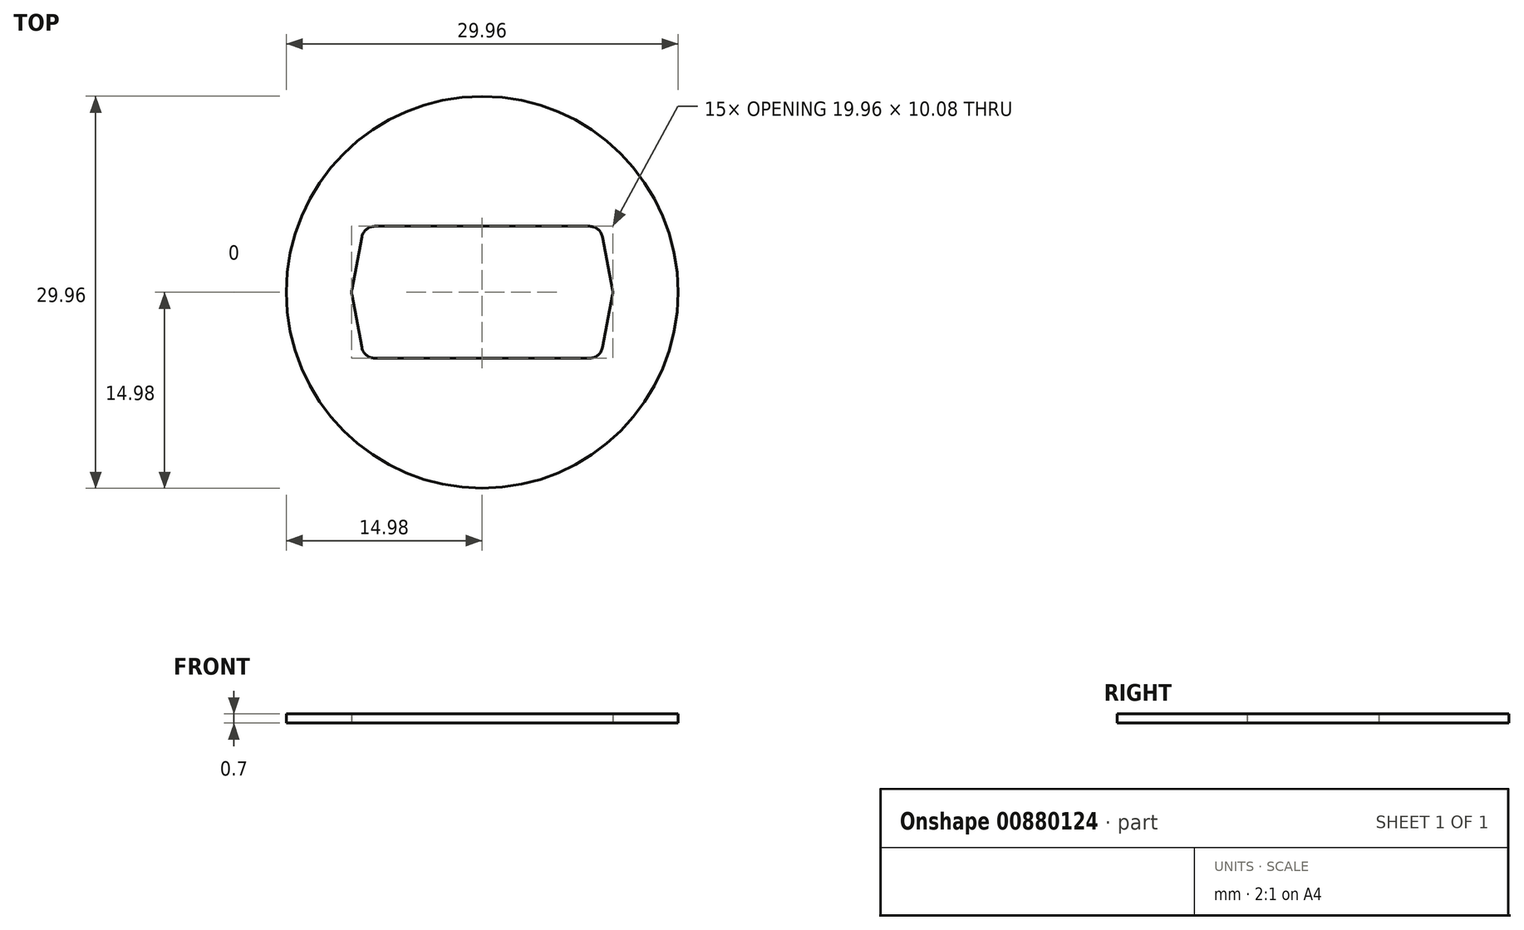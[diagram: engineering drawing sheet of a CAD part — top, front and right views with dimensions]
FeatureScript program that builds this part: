
annotation { "Feature Type Name" : "Feature", "Feature Type Description" : "" }
export const myFeature = defineFeature(function(context is Context, id is Id, definition is map)
    precondition{}
    {
        {
            var Q0;
            Q0=qCreatedBy(makeId("Top.planeOp"),FACE);
            var sketch = newSketch(context, id + "F0", { "sketchPlane" : qUnion([Q0])});
            skCircle(sketch, "E0", {"center": v(0, 0) * mm, "radius": 14.97 * mm});
            skLineSegment(sketch, "E1.bottom", {"start": v(8.21, 5.04) * mm, "end": v(-8.21, 5.04) * mm});
            skLineSegment(sketch, "E1.top", {"start": v(8.21, -5.04) * mm, "end": v(-8.21, -5.04) * mm});
            skLineSegment(sketch, "E1.left", {"start": v(9.04, 5.04) * mm, "end": v(9.04, -5.04) * mm, "construction": true});
            skLineSegment(sketch, "E1.right", {"start": v(-9.04, 5.04) * mm, "end": v(-9.04, -5.04) * mm, "construction": true});
            skLineSegment(sketch, "E2", {"start": v(-9.2, 4.23) * mm, "end": v(-9.96, 0.19) * mm});
            skLineSegment(sketch, "E3", {"start": v(-9.96, -0.19) * mm, "end": v(-9.2, -4.23) * mm});
            skLineSegment(sketch, "E4", {"start": v(9.2, 4.23) * mm, "end": v(9.96, 0.19) * mm});
            skLineSegment(sketch, "E5", {"start": v(9.96, -0.19) * mm, "end": v(9.2, -4.23) * mm});
            skPoint(sketch, "E6.visualSharp", {"position": v(-10, 0) * mm});
            skArc(sketch, "E6.filletArc", {"start": v(-9.96, 0.19) * mm, "mid": v(-9.98, 0) * mm, "end": v(-9.96, -0.19) * mm});
            skPoint(sketch, "E7.visualSharp", {"position": v(-9.04, 5.04) * mm});
            skArc(sketch, "E7.filletArc", {"start": v(-8.21, 5.04) * mm, "mid": v(-8.85, 4.81) * mm, "end": v(-9.2, 4.23) * mm});
            skPoint(sketch, "E8.visualSharp", {"position": v(-9.04, -5.04) * mm});
            skArc(sketch, "E8.filletArc", {"start": v(-9.2, -4.23) * mm, "mid": v(-8.85, -4.81) * mm, "end": v(-8.21, -5.04) * mm});
            skPoint(sketch, "E9.visualSharp", {"position": v(9.04, 5.04) * mm});
            skArc(sketch, "E9.filletArc", {"start": v(9.2, 4.23) * mm, "mid": v(8.85, 4.81) * mm, "end": v(8.21, 5.04) * mm});
            skPoint(sketch, "E10.visualSharp", {"position": v(10, 0) * mm});
            skArc(sketch, "E10.filletArc", {"start": v(9.96, -0.19) * mm, "mid": v(9.98, 0) * mm, "end": v(9.96, 0.19) * mm});
            skPoint(sketch, "E11.visualSharp", {"position": v(9.04, -5.04) * mm});
            skArc(sketch, "E11.filletArc", {"start": v(8.21, -5.04) * mm, "mid": v(8.85, -4.81) * mm, "end": v(9.2, -4.23) * mm});
            skSolve(sketch);
        }
        {
            var Q0;
            Q0 = qSketchRegion(id + "F0", true);
            extrude(context, id + "F1", {"entities" : qUnion([Q0]), "depth" : 0.7 * mm, "offsetDistance" : 25 * mm});
        }
    });
